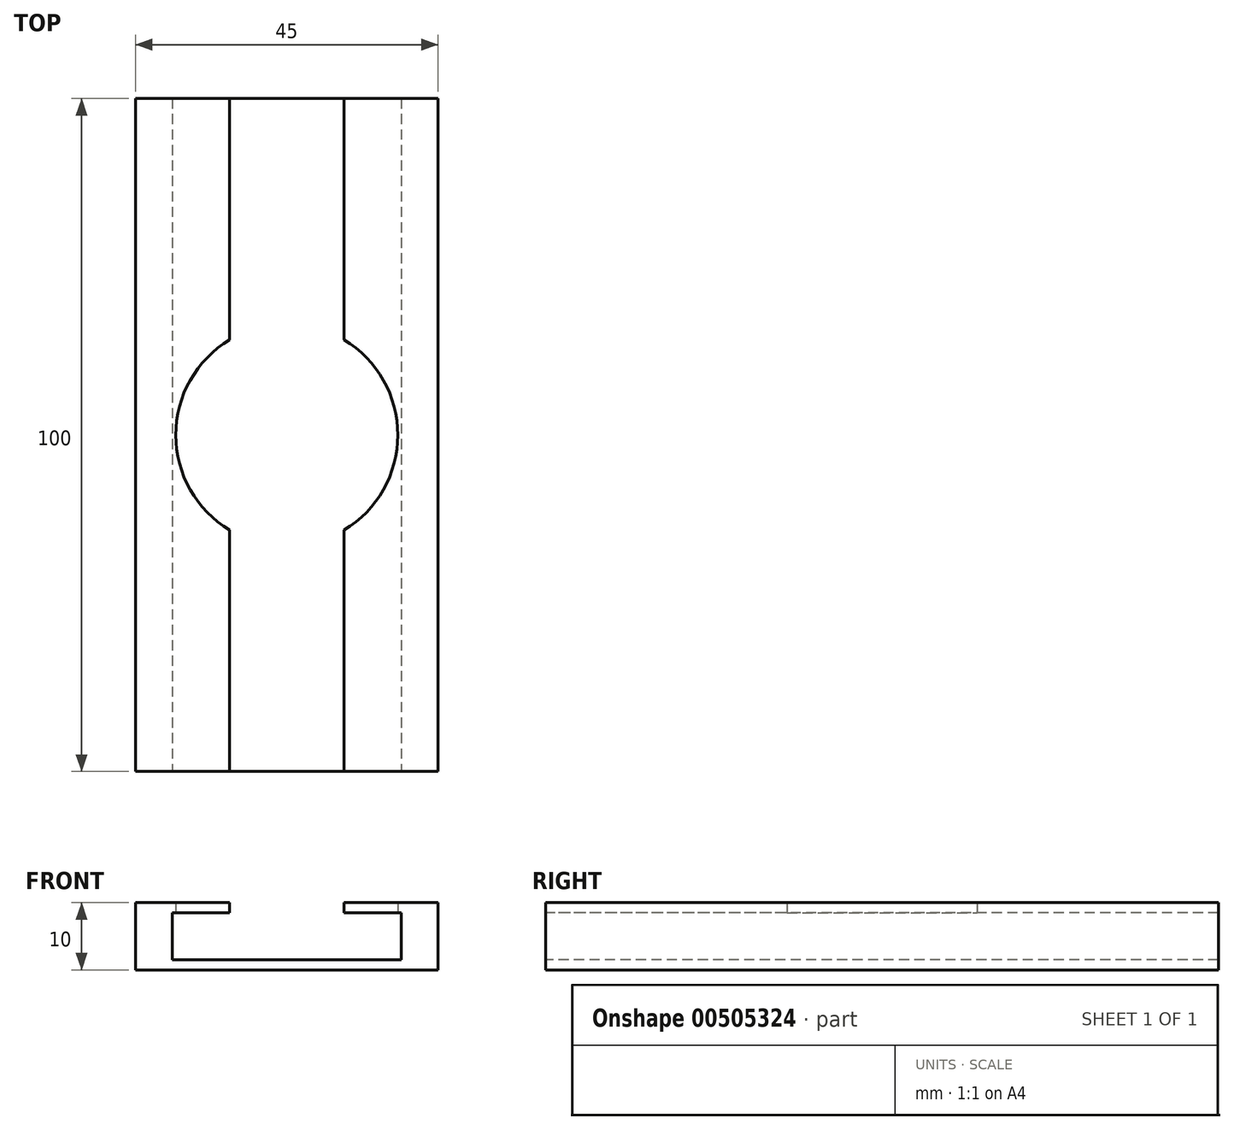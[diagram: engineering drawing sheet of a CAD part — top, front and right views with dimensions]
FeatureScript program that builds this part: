
annotation { "Feature Type Name" : "Feature", "Feature Type Description" : "" }
export const myFeature = defineFeature(function(context is Context, id is Id, definition is map)
    precondition{}
    {
        {
            var Q0;
            Q0=qCreatedBy(makeId("Top.planeOp"),FACE);
            var sketch = newSketch(context, id + "F0", { "sketchPlane" : qUnion([Q0])});
            skLineSegment(sketch, "E0.bottom", {"start": v(-56.34, 35.2) * mm, "end": v(-11.34, 35.2) * mm});
            skLineSegment(sketch, "E0.top", {"start": v(-56.34, -64.8) * mm, "end": v(-11.34, -64.8) * mm});
            skLineSegment(sketch, "E0.left", {"start": v(-56.34, 35.2) * mm, "end": v(-56.34, -64.8) * mm});
            skLineSegment(sketch, "E0.right", {"start": v(-11.34, 35.2) * mm, "end": v(-11.34, -64.8) * mm});
            skSolve(sketch);
        }
        {
            var Q0;
            Q0=makeQuery(id+"F0.imprint","IMPRINT",FACE,{"disambiguationData":[TD([[makeQuery(id+"F0.imprint","IMPRINT",EDGE,{"derivedFrom":sQuery(id+"F0.wireOp",EDGE,"E0.bottom")}),-1.0]])]});
            extrude(context, id + "F1", {"entities" : qUnion([Q0]), "depth" : 10 * mm});
        }
        {
            var Q0;
            Q0=makeQuery(id+"F1.opExtrude","CAP_FACE",FACE,{"disambiguationData":[OSD([sQuery(id+"F0.wireOp",EDGE,"E0.bottom"),sQuery(id+"F0.wireOp",EDGE,"E0.top"),sQuery(id+"F0.wireOp",EDGE,"E0.left"),sQuery(id+"F0.wireOp",EDGE,"E0.right")])],"isStart":false});
            var sketch = newSketch(context, id + "F2", { "sketchPlane" : qUnion([Q0])});
            skLineSegment(sketch, "E1.bottom", {"start": v(-42.34, -64.8) * mm, "end": v(-25.34, -64.8) * mm});
            skLineSegment(sketch, "E1.top", {"start": v(-42.34, 35.2) * mm, "end": v(-25.34, 35.2) * mm});
            skLineSegment(sketch, "E1.left", {"start": v(-42.34, -64.8) * mm, "end": v(-42.34, 35.2) * mm});
            skLineSegment(sketch, "E1.right", {"start": v(-25.34, -64.8) * mm, "end": v(-25.34, 35.2) * mm});
            skSolve(sketch);
        }
        {
            var Q0;
            Q0 = qSketchRegion(id + "F2", true);
            extrude(context, id + "F3", {"entities" : qUnion([Q0]), "operationType" : NewBodyOperationType.REMOVE, "oppositeDirection" : true, "depth" : 8.5 * mm});
        }
        {
            var Q0;
            Q0=qCreatedBy(makeId("Top.planeOp"),FACE);
            var sketch = newSketch(context, id + "F4", { "sketchPlane" : qUnion([Q0])});
            skLineSegment(sketch, "E2.bottom", {"start": v(-56.34, 35.2) * mm, "end": v(-22.34, 35.2) * mm});
            skLineSegment(sketch, "E2.top", {"start": v(-56.34, -64.8) * mm, "end": v(-22.34, -64.8) * mm});
            skLineSegment(sketch, "E2.left", {"start": v(-56.34, 35.2) * mm, "end": v(-56.34, -64.8) * mm});
            skLineSegment(sketch, "E2.right", {"start": v(-22.34, 35.2) * mm, "end": v(-22.34, -64.8) * mm});
            skSolve(sketch);
        }
        {
            var Q0;
            Q0=makeQuery(id+"F4.imprint","IMPRINT",FACE,{"disambiguationData":[TD([[makeQuery(id+"F4.imprint","IMPRINT",EDGE,{"derivedFrom":sQuery(id+"F4.wireOp",EDGE,"E2.bottom")}),-1.0]])]});
            extrude(context, id + "F5", {"entities" : qUnion([Q0]), "depth" : 7 * mm});
        }
        {
            var Q0;
            Q0=makeQuery(id+"F5.opExtrude","SWEPT_BODY",BODY,{"disambiguationData":[OSD([sQuery(id+"F4.wireOp",EDGE,"E2.bottom"),sQuery(id+"F4.wireOp",EDGE,"E2.top"),sQuery(id+"F4.wireOp",EDGE,"E2.left"),sQuery(id+"F4.wireOp",EDGE,"E2.right")])]});
            transform(context, id + "F6", {"entities" : qUnion([Q0]), "transformType" : TransformType.TRANSLATION_3D, "dx" : 5.5 * mm, "dy" : 0 * mm, "dz" : 1.5 * mm, "makeCopy" : false});
        }
        {
            var Q0;
            Q0=makeQuery(id+"F5.opExtrude","SWEPT_BODY",BODY,{"disambiguationData":[OSD([sQuery(id+"F4.wireOp",EDGE,"E2.bottom"),sQuery(id+"F4.wireOp",EDGE,"E2.top"),sQuery(id+"F4.wireOp",EDGE,"E2.left"),sQuery(id+"F4.wireOp",EDGE,"E2.right")])]});
            var Q1;
            Q1=makeQuery(id+"F1.opExtrude","SWEPT_BODY",BODY,{"disambiguationData":[OSD([sQuery(id+"F0.wireOp",EDGE,"E0.bottom"),sQuery(id+"F0.wireOp",EDGE,"E0.top"),sQuery(id+"F0.wireOp",EDGE,"E0.left"),sQuery(id+"F0.wireOp",EDGE,"E0.right")])]});
            booleanBodies(context, id + "F7", {"operationType" : BooleanOperationType.SUBTRACTION, "tools" : qUnion([Q0]), "targets" : qUnion([Q1])});
        }
        {
            var Q0;
            Q0=qCreatedBy(makeId("Top.planeOp"),FACE);
            var sketch = newSketch(context, id + "F8", { "sketchPlane" : qUnion([Q0])});
            skCircle(sketch, "E3", {"center": v(-33.84, -64.8) * mm, "radius": 16.5 * mm});
            skSolve(sketch);
        }
        {
            var Q0;
            Q0=makeQuery(id+"F8.imprint","IMPRINT",FACE,{"disambiguationData":[TD([[makeQuery(id+"F8.imprint","IMPRINT",EDGE,{"derivedFrom":sQuery(id+"F8.wireOp",EDGE,"E3")}),1.0]])]});
            extrude(context, id + "F9", {"entities" : qUnion([Q0]), "depth" : 10 * mm});
        }
        {
            var Q0;
            Q0=makeQuery(id+"F9.opExtrude","SWEPT_BODY",BODY,{"disambiguationData":[OSD([sQuery(id+"F8.wireOp",EDGE,"E3")])]});
            transform(context, id + "F10", {"entities" : qUnion([Q0]), "transformType" : TransformType.TRANSLATION_3D, "dx" : 0 * mm, "dy" : 50 * mm, "dz" : 4 * mm, "makeCopy" : false});
        }
        {
            var Q0;
            Q0=makeQuery(id+"F9.opExtrude","SWEPT_BODY",BODY,{"disambiguationData":[OSD([sQuery(id+"F8.wireOp",EDGE,"E3")])]});
            var Q1;
            Q1=makeQuery(id+"F1.opExtrude","SWEPT_BODY",BODY,{"disambiguationData":[OSD([sQuery(id+"F0.wireOp",EDGE,"E0.bottom"),sQuery(id+"F0.wireOp",EDGE,"E0.top"),sQuery(id+"F0.wireOp",EDGE,"E0.left"),sQuery(id+"F0.wireOp",EDGE,"E0.right")])]});
            booleanBodies(context, id + "F11", {"operationType" : BooleanOperationType.SUBTRACTION, "tools" : qUnion([Q0]), "targets" : qUnion([Q1])});
        }
    });
